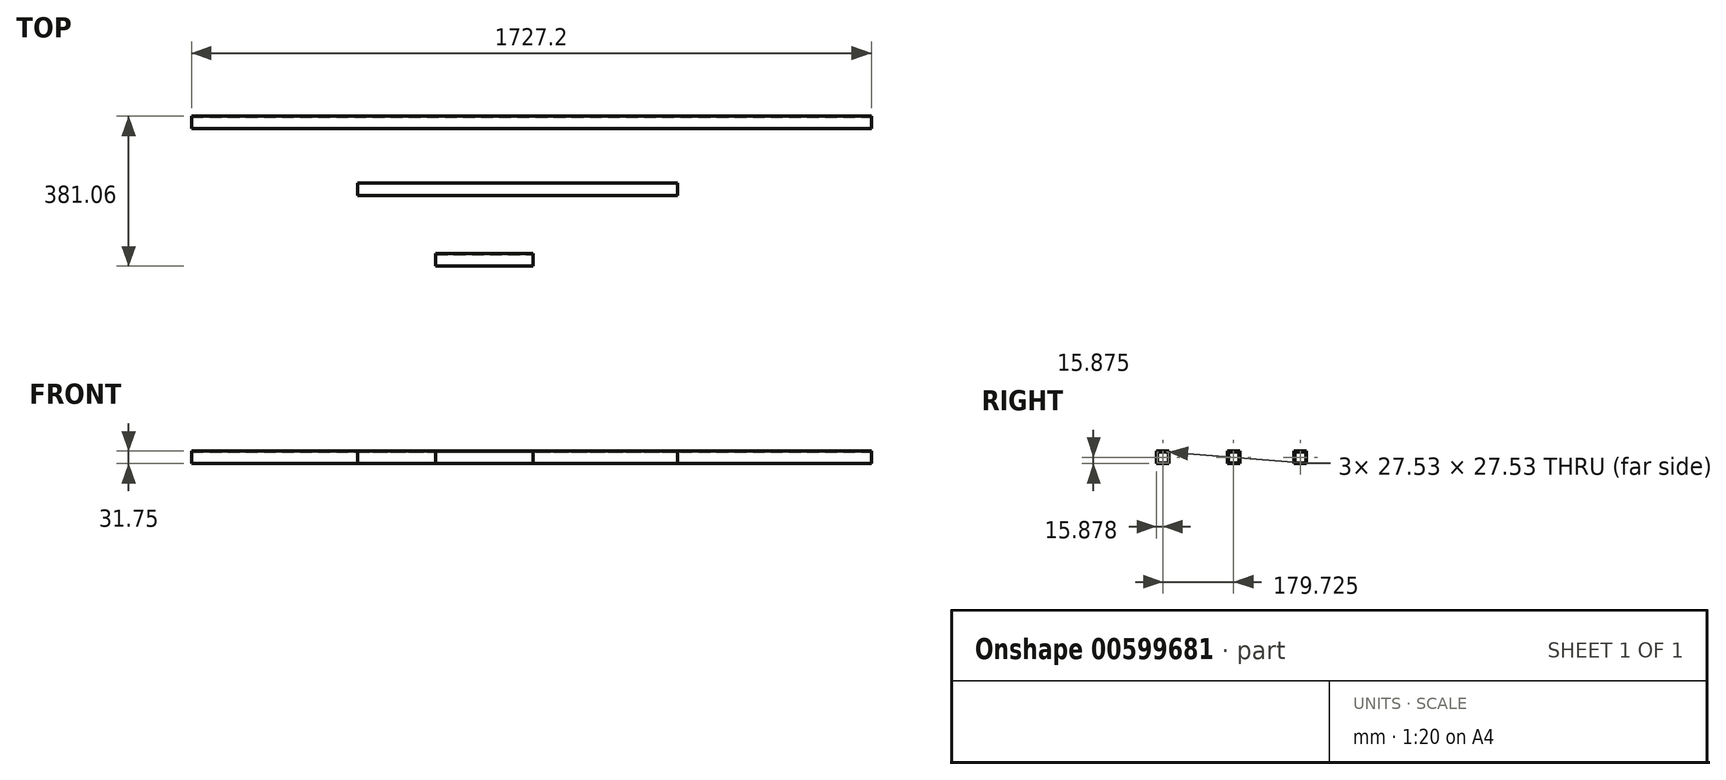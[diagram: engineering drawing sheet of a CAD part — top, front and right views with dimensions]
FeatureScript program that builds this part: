
annotation { "Feature Type Name" : "Feature", "Feature Type Description" : "" }
export const myFeature = defineFeature(function(context is Context, id is Id, definition is map)
    precondition{}
    {
        {
            var Q0;
            Q0=qCreatedBy(makeId("Top.planeOp"),FACE);
            var sketch = newSketch(context, id + "F0", { "sketchPlane" : qUnion([Q0])});
            skLineSegment(sketch, "E0.bottom", {"start": v(-401.88, 59.74) * mm, "end": v(410.92, 59.74) * mm});
            skLineSegment(sketch, "E0.top", {"start": v(-401.88, 27.99) * mm, "end": v(410.92, 27.99) * mm});
            skLineSegment(sketch, "E0.left", {"start": v(-401.88, 59.74) * mm, "end": v(-401.88, 27.99) * mm});
            skLineSegment(sketch, "E0.right", {"start": v(410.92, 59.74) * mm, "end": v(410.92, 27.99) * mm});
            skLineSegment(sketch, "E1.bottom", {"start": v(-824.38, 229.32) * mm, "end": v(902.82, 229.32) * mm});
            skLineSegment(sketch, "E1.top", {"start": v(-824.38, 197.57) * mm, "end": v(902.82, 197.57) * mm});
            skLineSegment(sketch, "E1.left", {"start": v(-824.38, 229.32) * mm, "end": v(-824.38, 197.57) * mm});
            skLineSegment(sketch, "E1.right", {"start": v(902.82, 229.32) * mm, "end": v(902.82, 197.57) * mm});
            skLineSegment(sketch, "E2.bottom", {"start": v(-204.15, -119.99) * mm, "end": v(43.5, -119.99) * mm});
            skLineSegment(sketch, "E2.top", {"start": v(-204.15, -151.74) * mm, "end": v(43.5, -151.74) * mm});
            skLineSegment(sketch, "E2.left", {"start": v(-204.15, -119.99) * mm, "end": v(-204.15, -151.74) * mm});
            skLineSegment(sketch, "E2.right", {"start": v(43.5, -119.99) * mm, "end": v(43.5, -151.74) * mm});
            skSolve(sketch);
        }
        {
            var Q0;
            Q0=makeQuery(id+"F0.imprint","IMPRINT",FACE,{"disambiguationData":[TD([[makeQuery(id+"F0.imprint","IMPRINT",EDGE,{"derivedFrom":sQuery(id+"F0.wireOp",EDGE,"E0.bottom")}),-1.0]])]});
            extrude(context, id + "F1", {"entities" : qUnion([Q0]), "depth" : 31.75 * mm, "offsetDistance" : 25.4 * mm});
        }
        {
            var Q0;
            Q0=makeQuery(id+"F1.opExtrude","SWEPT_FACE",FACE,{"disambiguationData":[OSD([sQuery(id+"F0.wireOp",EDGE,"E0.right")])]});
            var sketch = newSketch(context, id + "F2", { "sketchPlane" : qUnion([Q0])});
            skLineSegment(sketch, "E3.bottom", {"start": v(30.1, 29.64) * mm, "end": v(57.63, 29.64) * mm});
            skLineSegment(sketch, "E3.top", {"start": v(30.1, 2.1) * mm, "end": v(57.63, 2.1) * mm});
            skLineSegment(sketch, "E3.left", {"start": v(30.1, 29.64) * mm, "end": v(30.1, 2.1) * mm});
            skLineSegment(sketch, "E3.right", {"start": v(57.63, 29.64) * mm, "end": v(57.63, 2.1) * mm});
            skLineSegment(sketch, "E4", {"start": v(30.1, 2.1) * mm, "end": v(27.99, 2.1) * mm, "construction": true});
            skLineSegment(sketch, "E5", {"start": v(30.1, 2.1) * mm, "end": v(30.1, 0) * mm, "construction": true});
            skLineSegment(sketch, "E6", {"start": v(57.63, 29.64) * mm, "end": v(57.63, 31.75) * mm, "construction": true});
            skLineSegment(sketch, "E7", {"start": v(57.63, 29.64) * mm, "end": v(59.74, 29.64) * mm, "construction": true});
            skSolve(sketch);
        }
        {
            var Q0;
            Q0=makeQuery(id+"F2.imprint","IMPRINT",FACE,{"disambiguationData":[TD([[makeQuery(id+"F2.imprint","IMPRINT",EDGE,{"derivedFrom":sQuery(id+"F2.wireOp",EDGE,"E3.bottom")}),-1.0]])]});
            extrude(context, id + "F3", {"entities" : qUnion([Q0]), "operationType" : NewBodyOperationType.REMOVE, "oppositeDirection" : true, "depth" : 855.47 * mm, "offsetDistance" : 25.4 * mm});
        }
        {
            var Q0;
            Q0=makeQuery(id+"F0.imprint","IMPRINT",FACE,{"disambiguationData":[TD([[makeQuery(id+"F0.imprint","IMPRINT",EDGE,{"derivedFrom":sQuery(id+"F0.wireOp",EDGE,"E1.bottom")}),-1.0]])]});
            extrude(context, id + "F4", {"entities" : qUnion([Q0]), "depth" : 31.75 * mm, "offsetDistance" : 25.4 * mm});
        }
        {
            var Q0;
            Q0=makeQuery(id+"F4.opExtrude","SWEPT_FACE",FACE,{"disambiguationData":[OSD([sQuery(id+"F0.wireOp",EDGE,"E1.right")])]});
            var sketch = newSketch(context, id + "F5", { "sketchPlane" : qUnion([Q0])});
            skLineSegment(sketch, "E8.bottom", {"start": v(199.68, 29.64) * mm, "end": v(227.21, 29.64) * mm});
            skLineSegment(sketch, "E8.top", {"start": v(199.68, 2.1) * mm, "end": v(227.21, 2.1) * mm});
            skLineSegment(sketch, "E8.left", {"start": v(199.68, 29.64) * mm, "end": v(199.68, 2.1) * mm});
            skLineSegment(sketch, "E8.right", {"start": v(227.21, 29.64) * mm, "end": v(227.21, 2.1) * mm});
            skLineSegment(sketch, "E9", {"start": v(199.68, 2.1) * mm, "end": v(199.68, 0) * mm, "construction": true});
            skLineSegment(sketch, "E10", {"start": v(199.68, 2.1) * mm, "end": v(197.57, 2.1) * mm, "construction": true});
            skLineSegment(sketch, "E11", {"start": v(227.21, 29.64) * mm, "end": v(227.21, 31.75) * mm, "construction": true});
            skLineSegment(sketch, "E12", {"start": v(227.21, 29.64) * mm, "end": v(229.32, 29.64) * mm, "construction": true});
            skSolve(sketch);
        }
        {
            var Q0;
            Q0=makeQuery(id+"F5.imprint","IMPRINT",FACE,{"disambiguationData":[TD([[makeQuery(id+"F5.imprint","IMPRINT",EDGE,{"derivedFrom":sQuery(id+"F5.wireOp",EDGE,"E8.bottom")}),-1.0]])]});
            extrude(context, id + "F6", {"entities" : qUnion([Q0]), "operationType" : NewBodyOperationType.REMOVE, "oppositeDirection" : true, "depth" : 1783.08 * mm, "offsetDistance" : 25.4 * mm});
        }
        {
            var Q0;
            Q0=makeQuery(id+"F0.imprint","IMPRINT",FACE,{"disambiguationData":[TD([[makeQuery(id+"F0.imprint","IMPRINT",EDGE,{"derivedFrom":sQuery(id+"F0.wireOp",EDGE,"E2.bottom")}),-1.0]])]});
            extrude(context, id + "F7", {"entities" : qUnion([Q0]), "depth" : 31.75 * mm, "offsetDistance" : 25.4 * mm});
        }
        {
            var Q0;
            Q0=makeQuery(id+"F7.opExtrude","SWEPT_FACE",FACE,{"disambiguationData":[OSD([sQuery(id+"F0.wireOp",EDGE,"E2.right")])]});
            var sketch = newSketch(context, id + "F8", { "sketchPlane" : qUnion([Q0])});
            skLineSegment(sketch, "E13.bottom", {"start": v(-149.63, 29.64) * mm, "end": v(-122.1, 29.64) * mm});
            skLineSegment(sketch, "E13.top", {"start": v(-149.63, 2.1) * mm, "end": v(-122.1, 2.1) * mm});
            skLineSegment(sketch, "E13.left", {"start": v(-149.63, 29.64) * mm, "end": v(-149.63, 2.1) * mm});
            skLineSegment(sketch, "E13.right", {"start": v(-122.1, 29.64) * mm, "end": v(-122.1, 2.1) * mm});
            skLineSegment(sketch, "E14", {"start": v(-149.63, 2.1) * mm, "end": v(-151.74, 2.1) * mm, "construction": true});
            skLineSegment(sketch, "E15", {"start": v(-149.63, 2.1) * mm, "end": v(-149.63, 0) * mm, "construction": true});
            skLineSegment(sketch, "E16", {"start": v(-122.1, 29.64) * mm, "end": v(-122.1, 31.75) * mm, "construction": true});
            skLineSegment(sketch, "E17", {"start": v(-122.1, 29.64) * mm, "end": v(-119.99, 29.64) * mm, "construction": true});
            skSolve(sketch);
        }
        {
            var Q0;
            Q0=makeQuery(id+"F8.imprint","IMPRINT",FACE,{"disambiguationData":[TD([[makeQuery(id+"F8.imprint","IMPRINT",EDGE,{"derivedFrom":sQuery(id+"F8.wireOp",EDGE,"E13.bottom")}),-1.0]])]});
            extrude(context, id + "F9", {"entities" : qUnion([Q0]), "operationType" : NewBodyOperationType.REMOVE, "oppositeDirection" : true, "depth" : 254 * mm, "offsetDistance" : 25.4 * mm});
        }
    });
